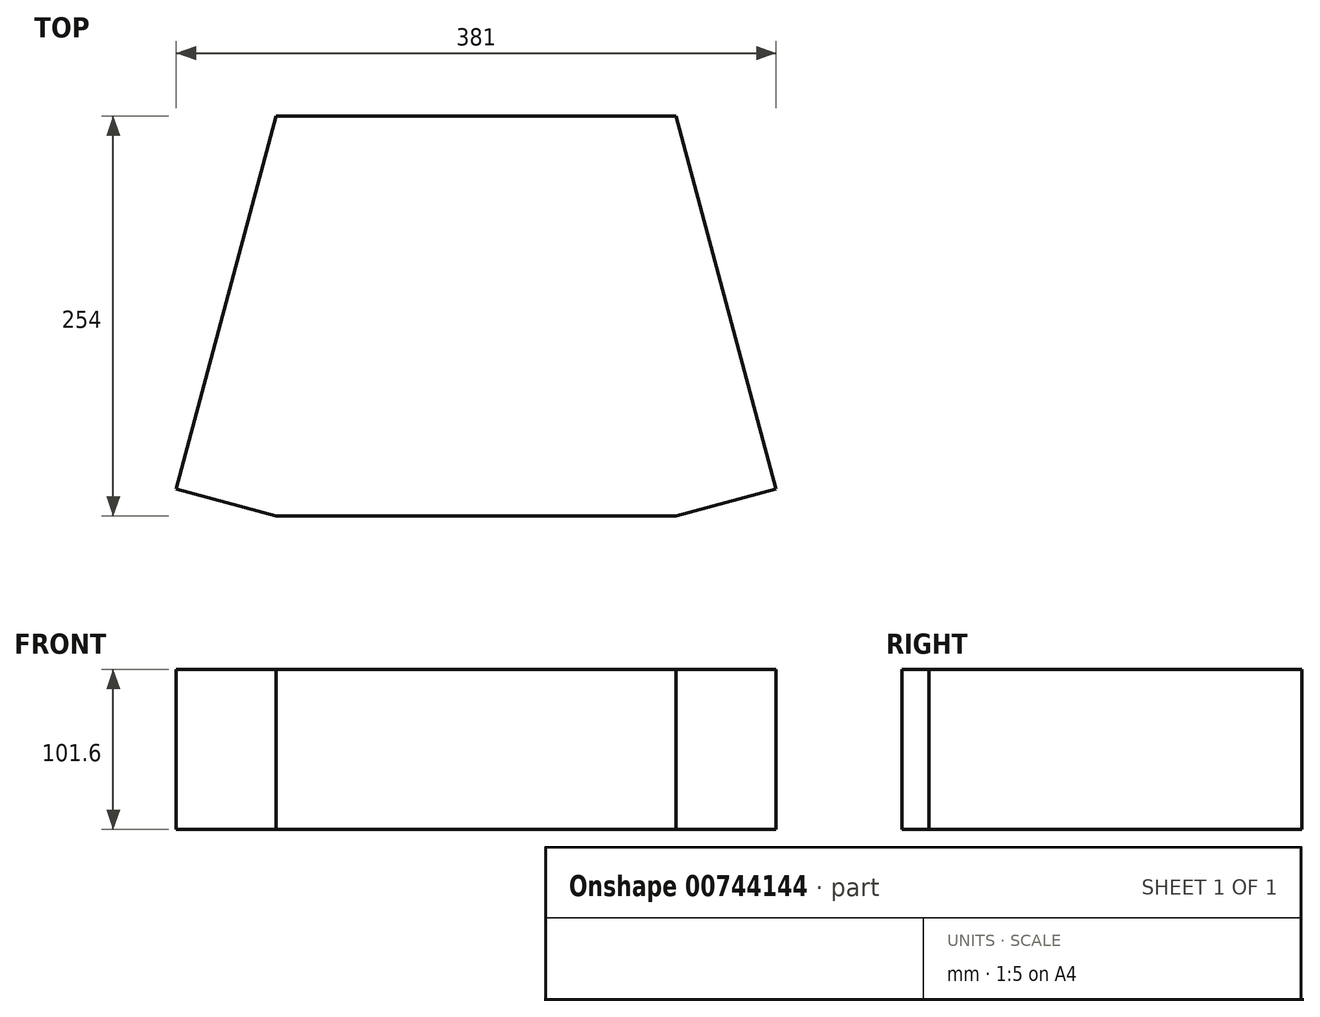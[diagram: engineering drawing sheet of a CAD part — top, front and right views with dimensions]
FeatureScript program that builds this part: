
annotation { "Feature Type Name" : "Feature", "Feature Type Description" : "" }
export const myFeature = defineFeature(function(context is Context, id is Id, definition is map)
    precondition{}
    {
        {
            var Q0;
            Q0=qCreatedBy(makeId("Top.planeOp"),FACE);
            var sketch = newSketch(context, id + "F0", { "sketchPlane" : qUnion([Q0])});
            skLineSegment(sketch, "E0", {"start": v(-138.33, -117.26) * mm, "end": v(-201.83, -100.24) * mm});
            skLineSegment(sketch, "E1", {"start": v(-138.33, 136.74) * mm, "end": v(-201.83, -100.24) * mm});
            skLineSegment(sketch, "E2", {"start": v(-138.33, 136.74) * mm, "end": v(115.67, 136.74) * mm});
            skLineSegment(sketch, "E3", {"start": v(115.67, 136.74) * mm, "end": v(179.17, -100.24) * mm});
            skLineSegment(sketch, "E4", {"start": v(115.67, -117.26) * mm, "end": v(179.17, -100.24) * mm});
            skLineSegment(sketch, "E5", {"start": v(115.67, -117.26) * mm, "end": v(-138.33, -117.26) * mm});
            skLineSegment(sketch, "E6", {"start": v(115.67, 136.74) * mm, "end": v(115.67, -117.26) * mm, "construction": true});
            skSolve(sketch);
        }
        {
            var Q0;
            Q0=makeQuery(id+"F0.imprint","IMPRINT",FACE,{"disambiguationData":[TD([[makeQuery(id+"F0.imprint","IMPRINT",EDGE,{"derivedFrom":sQuery(id+"F0.wireOp",EDGE,"E0")}),-1.0]])]});
            extrude(context, id + "F1", {"entities" : qUnion([Q0]), "depth" : 101.6 * mm, "offsetDistance" : 25.4 * mm});
        }
    });
